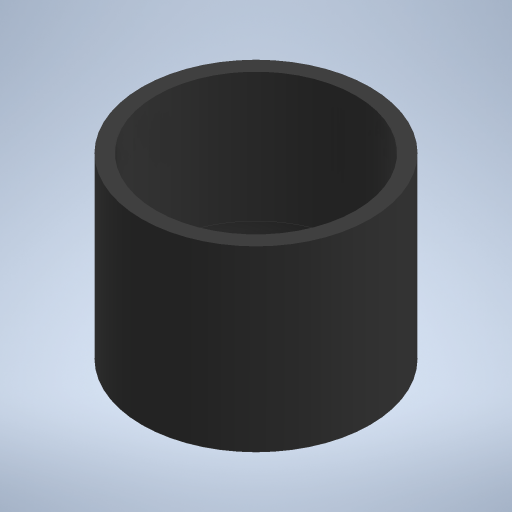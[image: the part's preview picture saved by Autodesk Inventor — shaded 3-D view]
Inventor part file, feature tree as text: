
AUTODESK INVENTOR PART (.ipt)
format: ipt  version: 2024 (Build 280153020, 153B)  size: 228,864 bytes
history: native  units: mm
features: sketch x2, revolve x1, extrude x1
ambient origin geometry x8: Origin, YZ Plane, XZ Plane, XY Plane, X Axis, Y Axis, Z Axis, Center Point
bodies: Solid1 (feature_tree)
feature tree (4):
  revolve  "Revolution1"  [1 undecoded]
  extrude  "Extrusion1"  Depth=25.0mm
  sketch  "Sketch1"  dims[d2=1.5mm d6=10.0mm]
  sketch  "Sketch3"  dims[d8=16.0mm d20=25.0mm d21=2.0mm d22=5.0mm d23=180.0deg d24=180.0deg d25=4.8mm d26=10.0mm d27=0.0mm d15=0.872665mm d16=0.872665mm]
note: 1 required parameter value undecoded (feature->parameter linkage not recoverable at this tier; creation-order binding heuristic only, values carry confidence <= 0.55)
